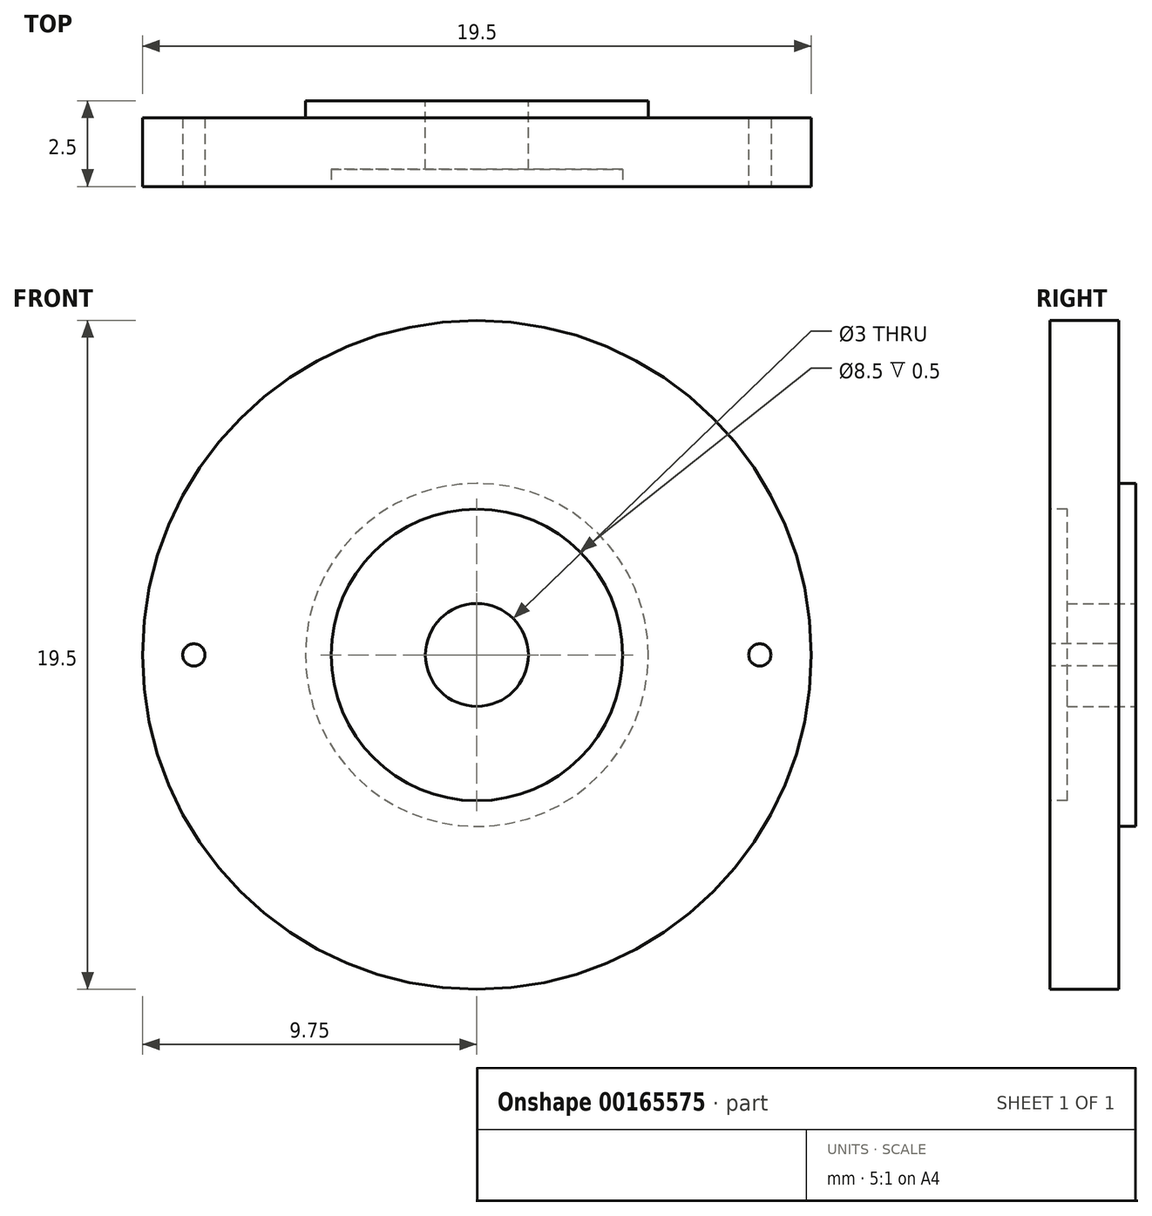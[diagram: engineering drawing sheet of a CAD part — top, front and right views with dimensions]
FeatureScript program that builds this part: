
annotation { "Feature Type Name" : "Feature", "Feature Type Description" : "" }
export const myFeature = defineFeature(function(context is Context, id is Id, definition is map)
    precondition{}
    {
        {
            var Q0;
            Q0=qCreatedBy(makeId("Front.planeOp"),FACE);
            var sketch = newSketch(context, id + "F0", { "sketchPlane" : qUnion([Q0])});
            skCircle(sketch, "E0", {"center": v(0, 0) * mm, "radius": 5 * mm});
            skCircle(sketch, "E1", {"center": v(0, 0) * mm, "radius": 1.5 * mm});
            skCircle(sketch, "E2", {"center": v(0, 0) * mm, "radius": 9.75 * mm});
            skSolve(sketch);
        }
        {
            var Q0;
            Q0=makeQuery(id+"F0.imprint","IMPRINT",FACE,{"disambiguationData":[TD([[makeQuery(id+"F0.imprint","IMPRINT",EDGE,{"derivedFrom":sQuery(id+"F0.wireOp",EDGE,"E0")}),-1.0]])]});
            var Q1;
            Q1=makeQuery(id+"F0.imprint","IMPRINT",FACE,{"disambiguationData":[TD([[makeQuery(id+"F0.imprint","IMPRINT",EDGE,{"derivedFrom":sQuery(id+"F0.wireOp",EDGE,"E0")}),1.0]])]});
            extrude(context, id + "F1", {"entities" : qUnion([Q0, Q1]), "depth" : 2.5 * mm});
        }
        {
            var Q0;
            Q0=makeQuery(id+"F0.imprint","IMPRINT",FACE,{"disambiguationData":[TD([[makeQuery(id+"F0.imprint","IMPRINT",EDGE,{"derivedFrom":sQuery(id+"F0.wireOp",EDGE,"E0")}),-1.0]])]});
            extrude(context, id + "F2", {"entities" : qUnion([Q0]), "operationType" : NewBodyOperationType.REMOVE, "depth" : 0.5 * mm});
        }
        {
            var Q0;
            Q0=makeQuery(id+"F1.opExtrude","CAP_FACE",FACE,{"disambiguationData":[OSD([sQuery(id+"F0.wireOp",EDGE,"E1"),sQuery(id+"F0.wireOp",EDGE,"E2")])],"isStart":false});
            var sketch = newSketch(context, id + "F3", { "sketchPlane" : qUnion([Q0])});
            skCircle(sketch, "E3", {"center": v(0, 0) * mm, "radius": 4.25 * mm});
            skCircle(sketch, "E4", {"center": v(8.25, 0) * mm, "radius": 0.33 * mm});
            skCircle(sketch, "E5", {"center": v(-8.25, 0) * mm, "radius": 0.33 * mm});
            skLineSegment(sketch, "E6", {"start": v(8.25, 0) * mm, "end": v(-8.25, 0) * mm, "construction": true});
            skSolve(sketch);
        }
        {
            var Q0;
            Q0=makeQuery(id+"F3.imprint","IMPRINT",FACE,{"disambiguationData":[TD([[makeQuery(id+"F3.imprint","IMPRINT",EDGE,{"derivedFrom":sQuery(id+"F3.wireOp",EDGE,"E3")}),1.0]])]});
            extrude(context, id + "F4", {"entities" : qUnion([Q0]), "operationType" : NewBodyOperationType.REMOVE, "oppositeDirection" : true, "depth" : 0.5 * mm});
        }
        {
            var Q0;
            Q0=makeQuery(id+"F3.imprint","IMPRINT",FACE,{"disambiguationData":[TD([[makeQuery(id+"F3.imprint","IMPRINT",EDGE,{"derivedFrom":sQuery(id+"F3.wireOp",EDGE,"E4")}),1.0]])]});
            var Q1;
            Q1=makeQuery(id+"F3.imprint","IMPRINT",FACE,{"disambiguationData":[TD([[makeQuery(id+"F3.imprint","IMPRINT",EDGE,{"derivedFrom":sQuery(id+"F3.wireOp",EDGE,"E5")}),1.0]])]});
            extrude(context, id + "F5", {"entities" : qUnion([Q0, Q1]), "operationType" : NewBodyOperationType.REMOVE, "endBound" : BoundingType.THROUGH_ALL, "oppositeDirection" : true, "depth" : 25 * mm});
        }
    });
